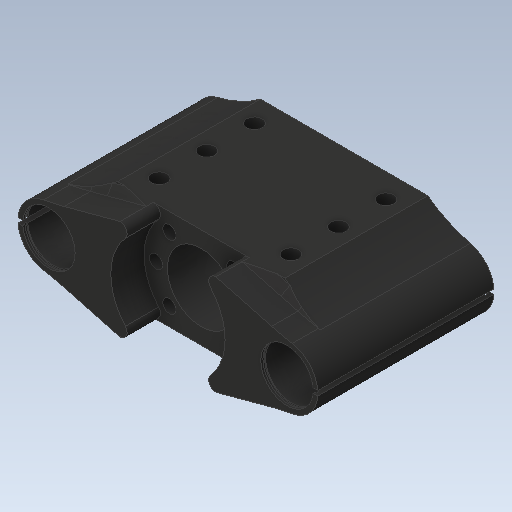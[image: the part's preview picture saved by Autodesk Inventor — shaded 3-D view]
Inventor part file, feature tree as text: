
AUTODESK INVENTOR PART (.ipt)
format: ipt  version: 2020 (Build 240168000, 168)  size: 549,888 bytes
history: native  units: mm
features: sketch x24, extrude x17, other x10, mirror x6, chamfer x5, fillet x3, pattern_circular x2, pattern_linear x1
ambient origin geometry x8: Origin, YZ Plane, XZ Plane, XY Plane, X Axis, Y Axis, Z Axis, Center Point
bodies: Body1 (feature_tree)
feature tree (68):
  other  "Bryła1"
  other  "Opisy"
  extrude  "Wyciągnięcie proste1"  Depth=22.0mm
  extrude  "Wyciągnięcie proste2"  Depth=26.0mm
  other  "Płaszczyzna konstrukcyjna1"
  extrude  "Wyciągnięcie proste3"  Depth=74.0mm TaperAngle=0.0deg
  extrude  "Wyciągnięcie proste4"  Depth=2.0mm
  other  "Płaszczyzna konstrukcyjna2"
  extrude  "Wyciągnięcie proste5"  Depth=1.0mm
  other  "Płaszczyzna konstrukcyjna3"
  mirror  "Odbij1"
  extrude  "Wyciągnięcie proste6"  Depth=80.0mm TaperAngle=0.0deg
  other  "Płaszczyzna konstrukcyjna4"
  mirror  "Odbij2"
  extrude  "Wyciągnięcie proste7"  [1 undecoded]
  sketch  "Szkic9"
  extrude  "Wyciągnięcie proste8"  Depth=22.0mm
  extrude  "Wyciągnięcie proste9"  Depth=19.0mm
  fillet  "Zaokrąglenie1"  Radius=6.0mm
  extrude  "Wyciągnięcie proste10"  Depth=2.0mm
  mirror  "Odbij3"
  chamfer  "Faza1"  Distance=6.0mm
  other  "Płaszczyzna konstrukcyjna5"
  chamfer  "Faza2"  [1 undecoded]
  chamfer  "Faza3"  Distance=23.0mm
  chamfer  "Faza4"  Distance=1.1mm
  fillet  "Zaokrąglenie2"  [1 undecoded]
  sketch  "Szkic13"
  extrude  "Wyciągnięcie proste13"  Depth=8.0mm
  extrude  "Wyciągnięcie proste14"  Depth=100.0mm
  pattern_circular  "Szyk kołowy3"  [2 undecoded]
  pattern_circular  "Szyk kołowy4"  Count=10  [1 undecoded]
  mirror  "Odbij5"
  extrude  "Wyciągnięcie proste15"  Depth=8.0mm
  extrude  "Wyciągnięcie proste16"  Depth=74.0mm TaperAngle=0.0deg
  extrude  "Wyciągnięcie proste17"  [1 undecoded]
  mirror  "Odbij6"
  fillet  "Zaokrąglenie3"  Radius=2.0mm
  chamfer  "Faza5"  Distance=74.0mm
  other  "Płaszczyzna konstrukcyjna6"
  sketch  "Szkic21"
  sketch  "Szkic22"
  extrude  "Wyciągnięcie proste18"  Depth=48.0mm
  pattern_linear  "Szyk prostokątny1"  Count1=5  [1 undecoded]
  mirror  "Odbij7"
  sketch  "Szkic24"
  sketch  "Szkic25"
  extrude  "Wyciągnięcie proste19"  Depth=14.0mm TaperAngle=0.0deg
  sketch  "Szkic27"
  other  "Płaszczyzna konstrukcyjna7"
  sketch  "Szkic28"
  sketch  "Szkic1"
  sketch  "Szkic2"
  sketch  "Szkic4"
  sketch  "Szkic5"
  sketch  "Szkic6"
  sketch  "Szkic7"
  sketch  "Szkic8"
  sketch  "Szkic10"
  sketch  "Szkic11"
  sketch  "Szkic12"
  sketch  "Szkic15"
  sketch  "Szkic18"
  sketch  "Szkic19"
  sketch  "Szkic20"
  sketch  "Szkic23"
  sketch  "Szkic26"
  other  "Wymiar liniowy 1"
note: 8 required parameter values undecoded (feature->parameter linkage not recoverable at this tier; creation-order binding heuristic only, values carry confidence <= 0.55)
